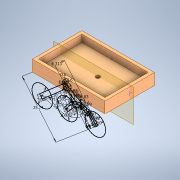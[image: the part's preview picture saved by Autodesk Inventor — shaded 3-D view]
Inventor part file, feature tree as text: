
AUTODESK INVENTOR PART (.ipt)
format: ipt  version: 2020 (Build 240168000, 168)  size: 233,472 bytes
history: native  units: in
note: dims shown in document units (in); Inventor stores cm internally (conversion verified against a paired STEP export)
features: sketch x7, extrude x4, plane x1
ambient origin geometry x8: Origin, YZ Plane, XZ Plane, XY Plane, X Axis, Y Axis, Z Axis, Center Point
bodies: Body1 (feature_tree)
feature tree (12):
  extrude  "Extrusion3"  Depth=9.5276in
  extrude  "Extrusion7"  Depth=0.7874in
  extrude  "Extrusion8"  Depth=0.5906in
  extrude  "Extrusion9"  Depth=1.378in TaperAngle=0.0deg
  sketch  "Sketch10"  dims[d27=0.2362in]
  plane  "Work Plane1"
  sketch  "Sketch13"  dims[d28=0.0in d29=0.0in]
  sketch  "Sketch14"  dims[d34=0.7874in d35=6.2992in d36=0.7874in d38=0.3937in d39=0.7874in d42=0.3937in d43=0.7874in d46=0.2362in d47=0.2362in d48=0.2362in d53=1.7717in d55=0.3937in d56=0.7874in d57=1.9685in d58=0.3937in d59=0.3937in d60=0.3937in d61=0.7874in d62=0.3937in d63=0.3937in d64=0.3937in d65=0.7874in d66=0.2362in d67=0.2362in d68=1.9685in d69=0.3937in d70=0.23in d72=0.4588in d73=0.166in d74=0.6868in d75=2.4679in d76=6.7315in d77=2.4855in d78=2.1476in d79=0.3937in d80=10.1339in d83=0.2362in d84=0.7463in d85=0.7063in d86=0.4455in d87=1.0639in d88=0.7874in d89=3.937in d90=3.0768in d91=0.397in d92=0.397in d93=0.3839in d94=0.377in d95=0.3002in d96=1.2409in d97=1.2409in d98=0.3862in d99=3.937in d100=3.937in d101=3.937in d102=0.9024in d103=2.525in d104=0.6065in d105=4.136in d106=0.5418in d18=0.1969in d19=0.0344in]
  sketch  "Sketch3"  dims[d4=2.1654in d5=9.5276in]
  sketch  "Sketch7"  dims[d6=13.9764in d7=0.0in d20=0.7874in]
  sketch  "Sketch8"  dims[d21=0.0in d22=0.0in d23=0.5906in]
  sketch  "Sketch9"  dims[d24=0.5906in d25=1.378in d26=0.0in]
